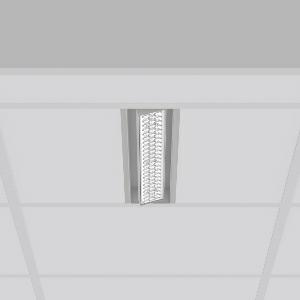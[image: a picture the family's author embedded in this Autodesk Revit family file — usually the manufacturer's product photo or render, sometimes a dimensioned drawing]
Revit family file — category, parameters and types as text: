
# Revit family: tx-move_901728_004_2_76_1993
name_source: partatom
category: Lighting Fixtures
units: mm (PartAtom-declared; Revit-internal decimal feet)

## family parameters
Cut with Voids When Loaded = No
Host = Face
Light Source = No
Part Type = Normal
Room Calculation Point = No
Round Connector Dimension = Use Diameter
Shared = No

## types (1)
- MultiLumen 1 (1 x LED Modul 927, 1950 lm, 2700)
    Apparent Load = 16 VA
    Approval mark = CE
    CIE Flux Codes = 88 96 99 100 100
    Color Rendering = 92
    Color Temperature = 2700
    Default Elevation = 1800 mm
    Description = Series: TX-MOVE
Einlege/Einbau-Flächenstrahler. Housing: sheet steel, powder-coated. Swivel range: 90°. High-efficiency LED units with optimum light control thanks to clear plastic (PC) lens optics. Spezielle Mikrostrukturen reduzieren Gelbsaum. Symmetrical light distribution. Best colour rendering with CRI >90 for fresh products and coloured textiles. Suitable for laying in grid ceiling module 625. Connected converter included in separate gearbox.Suitable for through-wiring.MultiLumen: Luminous flux adjustable in 3 steps. Accessories: Mounting frame for installation in suspended ceilings. Environmentally friendly and resource-saving due to replaceable and recyclable components. 
Colour: silver, matt (approx. RAL 9006)
Length: 622 mm
Width: 116 mm
Height: 39 mm
Cut-out length: 602 mm
Cut-out width: 98 mm
Recess height: 100 mm
Lamp: LED
Socket: without socket
Colour temperature: 2700K
Colour rendering index (CRI): 90
System power: 16 W
Rated luminous flux: 1950 lm
Luminous efficiency: 122 lm/W
System power 2: 23 W
Rated luminous flux 2: 2750 lm
Luminous efficiency 2: 120 lm/W
System power 3: 31 W
Rated luminous flux 3: 3500 lm
Luminous efficiency 3: 113 lm/W
Control gear: Dimmable EVG, DALI
Protection class: I
Type of protection: IP 20
    Height = 0 mm  [stored 0 ft]
    Lamp = 1 x LED Modul 927
    Lamp Light Flux = 1950 lm
    Lamp count = 1
    Length = 622 mm
    Lifetime = 50000 h
    Luminous efficacy = 122 lm/W
    Manufacturer = RZB
    ModVariant = No
    Model = 901728.004.2.76
    Mounting Place = Ceiling, Wall
    Mounting Type = Recessed
    Number of Poles = 1
    OnlyDefault = Yes
    Power Factor = 1
    Product Name = TX-MOVE
    Product group = Recessed projectors
    ProductGroupID = 401
    Protection Class = Protection class I
    Protection Degree = IP 20
    RLX_Detail_Level = 1
    RLX_Emergency_Light_Flux = 0 lm
    RLX_Emergency_Type = 0
    RLX_Emergency_Type_DB = No
    RlxData = <blob elided: 27497 chars, md5=76db4116>
    Socket = socket
    Standby Power = 0 W
    System Light Flux = 1950 lm
    System Power = 16 W
    Type Comments = MultiLumen 1
    Type Image = 901729.004.jpg
    URL = http://relux.com
    VarID = multilumen_1
    Voltage = 230 V
    Voltage Range = 220-240 V
    Weight = 0.00 kg
    Width = 116 mm

note: [stored X ft] marks values corroborated as IEEE doubles in the binary element streams (Revit-internal decimal feet)

## geometry (parser evidence)
native form markers: Blend x4, Sweep x14
no freeform markers — native parametric forms only
